# Revit family: RKB 500X250 B1 ErP AC_7470047
name_source: partatom
category: Mechanical Equipment
revit_build: Autodesk Revit MEP 2014 (Build: 20130308_1515(x64)
units: mm (PartAtom-declared; Revit-internal decimal feet)

## types (1)
- RKB 500X250 B1 ErP AC
    Capacitor = 5 μF
    Connector Height = 250 mm  [stored 0.82021 ft]
    Connector Width = 500 mm  [stored 1.64042 ft]
    Current = 1 A
    Depth = 543 mm  [stored 1.7815 ft]
    Description = UNINSULATED DUCT FANS WITH RECTANGULAR CONNECTIONS
    Frequency = 50 Hz
    Height = 293 mm
    Main Material = Steel, Galvanized
    Max. temperature of transported air = 70 °C
    Max. temperature of transported air when speed controlled = 70 °C
    Phase = 1
    Power = 168 W
    Sound pressure level at 3 m = 58 dB(A)
    Speed = 2680 rpm
    Voltage = 230 V
    Voltage range = 220-240 V
    Weight = 14.70 kg
    Width = 532 mm  [stored 1.74541 ft]
    Wiring diagram = 4040001

note: [stored X ft] marks values corroborated as IEEE doubles in the binary element streams (Revit-internal decimal feet)

## geometry (parser evidence)
native form markers: Sweep x4
no freeform markers — native parametric forms only
